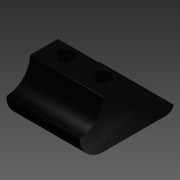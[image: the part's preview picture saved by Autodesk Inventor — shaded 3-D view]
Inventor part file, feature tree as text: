
AUTODESK INVENTOR PART (.ipt)
format: ipt  version: 2015 (Build 190159000, 159)  size: 157,184 bytes
history: native  units: mm
features: fillet x3, sketch x3, extrude x2, other x1, hole x1
ambient origin geometry x8: Origin, YZ Plane, XZ Plane, XY Plane, X Axis, Y Axis, Z Axis, Center Point
bodies: Body1 (feature_tree)
feature tree (10):
  other  "Bryła1"
  extrude  "Wyciągnięcie proste1"  Depth=28.0mm
  extrude  "Wyciągnięcie proste2"  Depth=36.0mm
  fillet  "Zaokrąglenie1"  Radius=18.0mm
  fillet  "Zaokrąglenie2"  Radius=18.0mm
  fillet  "Zaokrąglenie3"  Radius=32.0mm
  hole  "Otwór1"  [1 undecoded]
  sketch  "Szkic1"
  sketch  "Szkic3"
  sketch  "Szkic4"
note: 1 required parameter value undecoded (feature->parameter linkage not recoverable at this tier; creation-order binding heuristic only, values carry confidence <= 0.55)
